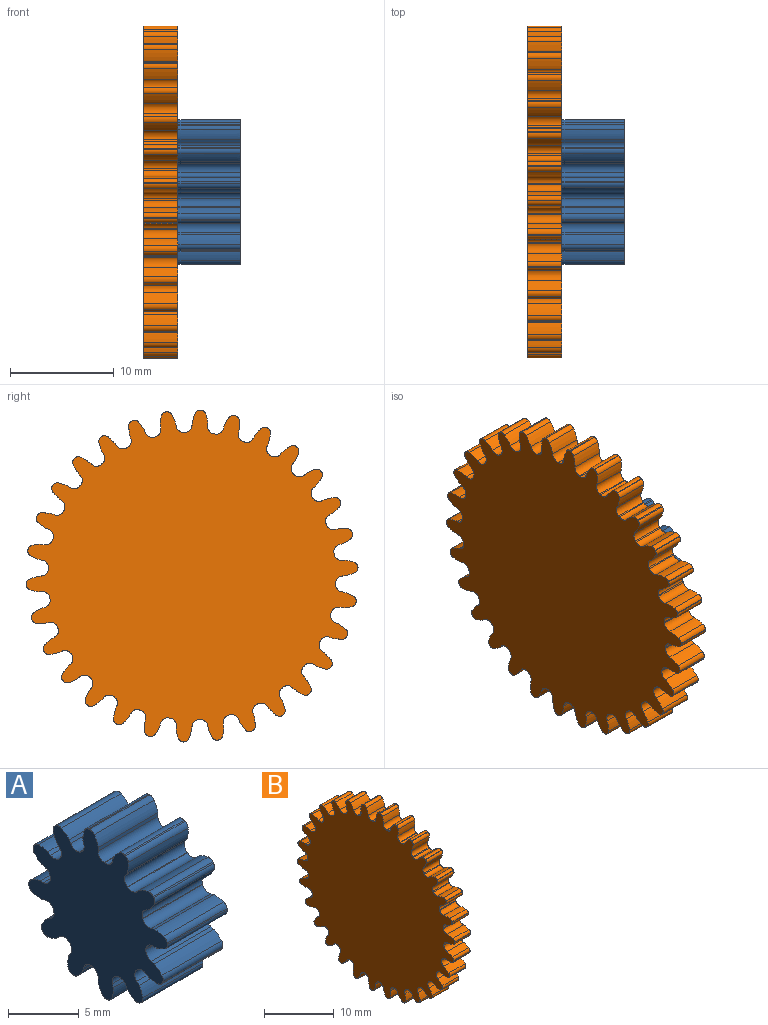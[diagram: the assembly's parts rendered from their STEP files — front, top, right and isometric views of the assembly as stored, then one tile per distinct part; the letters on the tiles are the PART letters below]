
ASSEMBLY  parts=2 mates=1
PART A: 122 faces, bbox 6x13.9x13.9 mm
  f0: cylinder r=4.84mm len=6mm, axis (-1,0,0), area 0.2mm2, adj f72,f73,f75,f76
  f1: plane 6x0.3mm, normal (0,-0.26,0.97), area 1.9mm2, adj f2,f72,f73,f74
  f2: extruded ~6x0.79mm, area 6mm2, adj f1,f72,f73,f98
  f3: cylinder r=7mm len=6mm, axis (-1,0,0), area 0.7mm2, adj f72,f73,f98,f99
  f4: extruded ~6x0.99mm, area 6mm2, adj f5,f72,f73,f99
  f5: plane 6x0.27mm, normal (0,0.5,-0.87), area 1.9mm2, adj f4,f72,f73,f75
  f6: cylinder r=4.84mm len=6mm, axis (-1,0,0), area 0.2mm2, adj f72,f73,f77,f78
  f7: plane 6x0.22mm, normal (0,-0.71,0.71), area 1.9mm2, adj f8,f72,f73,f76
  f8: extruded ~6x0.92mm, area 6mm2, adj f7,f72,f73,f100
  f9: cylinder r=7mm len=6mm, axis (-1,0,0), area 0.7mm2, adj f72,f73,f100,f101
  f10: extruded ~6x0.79mm, area 6mm2, adj f11,f72,f73,f101
  f11: plane 6x0.27mm, normal (0,0.87,-0.5), area 1.9mm2, adj f10,f72,f73,f77
  f12: cylinder r=4.84mm len=6mm, axis (-1,0,0), area 0.2mm2, adj f72,f73,f79,f80
  f13: plane 6x0.3mm, normal (0,-0.97,0.26), area 1.9mm2, adj f14,f72,f73,f78
  f14: extruded ~6x0.99mm, area 6mm2, adj f13,f72,f73,f102
  f15: cylinder r=7mm len=6mm, axis (-1,0,0), area 0.7mm2, adj f72,f73,f102,f103
  f16: extruded ~6x0.92mm, area 6mm2, adj f17,f72,f73,f103
  f17: plane 6x0.31mm, normal (0,1,0), area 1.9mm2, adj f16,f72,f73,f79
  f18: cylinder r=4.84mm len=6mm, axis (-1,0,0), area 0.2mm2, adj f72,f73,f81,f82
  f19: plane 6x0.3mm, normal (0,-0.97,-0.26), area 1.9mm2, adj f20,f72,f73,f80
  f20: extruded ~6x0.79mm, area 6mm2, adj f19,f72,f73,f104
  f21: cylinder r=7mm len=6mm, axis (-1,0,0), area 0.7mm2, adj f72,f73,f104,f105
  f22: extruded ~6x0.99mm, area 6mm2, adj f23,f72,f73,f105
  f23: plane 6x0.27mm, normal (0,0.87,0.5), area 1.9mm2, adj f22,f72,f73,f81
  f24: cylinder r=4.84mm len=6mm, axis (-1,0,0), area 0.2mm2, adj f72,f73,f83,f84
  f25: plane 6x0.22mm, normal (0,-0.71,-0.71), area 1.9mm2, adj f26,f72,f73,f82
  f26: extruded ~6x0.92mm, area 6mm2, adj f25,f72,f73,f106
  f27: cylinder r=7mm len=6mm, axis (-1,0,0), area 0.7mm2, adj f72,f73,f106,f107
  f28: extruded ~6x0.79mm, area 6mm2, adj f29,f72,f73,f107
  f29: plane 6x0.27mm, normal (0,0.5,0.87), area 1.9mm2, adj f28,f72,f73,f83
  f30: cylinder r=4.84mm len=6mm, axis (-1,0,0), area 0.2mm2, adj f72,f73,f85,f86
  f31: plane 6x0.3mm, normal (0,-0.26,-0.97), area 1.9mm2, adj f32,f72,f73,f84
  f32: extruded ~6x0.99mm, area 6mm2, adj f31,f72,f73,f108
  f33: cylinder r=7mm len=6mm, axis (-1,0,0), area 0.7mm2, adj f72,f73,f108,f109
  f34: extruded ~6x0.92mm, area 6mm2, adj f35,f72,f73,f109
  f35: plane 6x0.31mm, normal (0,0,1), area 1.9mm2, adj f34,f72,f73,f85
  f36: cylinder r=4.84mm len=6mm, axis (-1,0,0), area 0.2mm2, adj f72,f73,f87,f88
  f37: plane 6x0.3mm, normal (0,0.26,-0.97), area 1.9mm2, adj f38,f72,f73,f86
  f38: extruded ~6x0.79mm, area 6mm2, adj f37,f72,f73,f110
  f39: cylinder r=7mm len=6mm, axis (-1,0,0), area 0.7mm2, adj f72,f73,f110,f111
  f40: extruded ~6x0.99mm, area 6mm2, adj f41,f72,f73,f111
  f41: plane 6x0.27mm, normal (0,-0.5,0.87), area 1.9mm2, adj f40,f72,f73,f87
  f42: cylinder r=4.84mm len=6mm, axis (-1,0,0), area 0.2mm2, adj f72,f73,f89,f90
  f43: plane 6x0.22mm, normal (0,0.71,-0.71), area 1.9mm2, adj f44,f72,f73,f88
  f44: extruded ~6x0.92mm, area 6mm2, adj f43,f72,f73,f112
  f45: cylinder r=7mm len=6mm, axis (-1,0,0), area 0.7mm2, adj f72,f73,f112,f113
  f46: extruded ~6x0.79mm, area 6mm2, adj f47,f72,f73,f113
  f47: plane 6x0.27mm, normal (0,-0.87,0.5), area 1.9mm2, adj f46,f72,f73,f89
  f48: cylinder r=4.84mm len=6mm, axis (-1,0,0), area 0.2mm2, adj f72,f73,f91,f92
  f49: plane 6x0.3mm, normal (0,0.97,-0.26), area 1.9mm2, adj f50,f72,f73,f90
  f50: extruded ~6x0.99mm, area 6mm2, adj f49,f72,f73,f114
  f51: cylinder r=7mm len=6mm, axis (-1,0,0), area 0.7mm2, adj f72,f73,f114,f115
  f52: extruded ~6x0.92mm, area 6mm2, adj f53,f72,f73,f115
  f53: plane 6x0.31mm, normal (0,-1,0), area 1.9mm2, adj f52,f72,f73,f91
  f54: cylinder r=4.84mm len=6mm, axis (-1,0,0), area 0.2mm2, adj f72,f73,f93,f94
  f55: plane 6x0.3mm, normal (0,0.97,0.26), area 1.9mm2, adj f56,f72,f73,f92
  f56: extruded ~6x0.79mm, area 6mm2, adj f55,f72,f73,f116
  f57: cylinder r=7mm len=6mm, axis (-1,0,0), area 0.7mm2, adj f72,f73,f116,f117
  f58: extruded ~6x0.99mm, area 6mm2, adj f59,f72,f73,f117
  f59: plane 6x0.27mm, normal (0,-0.87,-0.5), area 1.9mm2, adj f58,f72,f73,f93
  f60: cylinder r=4.84mm len=6mm, axis (-1,0,0), area 0.2mm2, adj f72,f73,f95,f96
  f61: plane 6x0.22mm, normal (0,0.71,0.71), area 1.9mm2, adj f62,f72,f73,f94
  f62: extruded ~6x0.92mm, area 6mm2, adj f61,f72,f73,f118
  f63: cylinder r=7mm len=6mm, axis (-1,0,0), area 0.7mm2, adj f72,f73,f118,f119
  f64: extruded ~6x0.79mm, area 6mm2, adj f65,f72,f73,f119
  f65: plane 6x0.27mm, normal (0,-0.5,-0.87), area 1.9mm2, adj f64,f72,f73,f95
  f66: cylinder r=4.84mm len=6mm, axis (-1,0,0), area 0.2mm2, adj f72,f73,f74,f97
  f67: plane 6x0.3mm, normal (0,0.26,0.97), area 1.9mm2, adj f68,f72,f73,f96
  f68: extruded ~6x0.99mm, area 6mm2, adj f67,f72,f73,f120
  f69: cylinder r=7mm len=6mm, axis (-1,0,0), area 0.7mm2, adj f72,f73,f120,f121
  f70: extruded ~6x0.92mm, area 6mm2, adj f71,f72,f73,f121
  f71: plane 6x0.31mm, normal (0,0,-1), area 1.9mm2, adj f70,f72,f73,f97
  f72: plane 13.9x13.9mm, normal (1,0,0), area 109.3mm2, adj f0,f1,f2,f3,f4,f5,f6,f7
  f73: plane 13.9x13.9mm, normal (-1,0,0), area 109.3mm2, adj f0,f1,f2,f3,f4,f5,f6,f7
  f74: cylinder r=0.7mm len=6mm, axis (-1,0,0), area 6.1mm2, adj f1,f66,f72,f73
  f75: cylinder r=0.7mm len=6mm, axis (-1,0,0), area 6.1mm2, adj f0,f5,f72,f73
  f76: cylinder r=0.7mm len=6mm, axis (-1,0,0), area 6.1mm2, adj f0,f7,f72,f73
  f77: cylinder r=0.7mm len=6mm, axis (-1,0,0), area 6.1mm2, adj f6,f11,f72,f73
  f78: cylinder r=0.7mm len=6mm, axis (-1,0,0), area 6.1mm2, adj f6,f13,f72,f73
  f79: cylinder r=0.7mm len=6mm, axis (-1,0,0), area 6.1mm2, adj f12,f17,f72,f73
  f80: cylinder r=0.7mm len=6mm, axis (-1,0,0), area 6.1mm2, adj f12,f19,f72,f73
  f81: cylinder r=0.7mm len=6mm, axis (-1,0,0), area 6.1mm2, adj f18,f23,f72,f73
  f82: cylinder r=0.7mm len=6mm, axis (-1,0,0), area 6.1mm2, adj f18,f25,f72,f73
  f83: cylinder r=0.7mm len=6mm, axis (-1,0,0), area 6.1mm2, adj f24,f29,f72,f73
  f84: cylinder r=0.7mm len=6mm, axis (-1,0,0), area 6.1mm2, adj f24,f31,f72,f73
  f85: cylinder r=0.7mm len=6mm, axis (-1,0,0), area 6.1mm2, adj f30,f35,f72,f73
  f86: cylinder r=0.7mm len=6mm, axis (-1,0,0), area 6.1mm2, adj f30,f37,f72,f73
  f87: cylinder r=0.7mm len=6mm, axis (-1,0,0), area 6.1mm2, adj f36,f41,f72,f73
  f88: cylinder r=0.7mm len=6mm, axis (-1,0,0), area 6.1mm2, adj f36,f43,f72,f73
  f89: cylinder r=0.7mm len=6mm, axis (-1,0,0), area 6.1mm2, adj f42,f47,f72,f73
  f90: cylinder r=0.7mm len=6mm, axis (-1,0,0), area 6.1mm2, adj f42,f49,f72,f73
  f91: cylinder r=0.7mm len=6mm, axis (-1,0,0), area 6.1mm2, adj f48,f53,f72,f73
  f92: cylinder r=0.7mm len=6mm, axis (-1,0,0), area 6.1mm2, adj f48,f55,f72,f73
  f93: cylinder r=0.7mm len=6mm, axis (-1,0,0), area 6.1mm2, adj f54,f59,f72,f73
  f94: cylinder r=0.7mm len=6mm, axis (-1,0,0), area 6.1mm2, adj f54,f61,f72,f73
  f95: cylinder r=0.7mm len=6mm, axis (-1,0,0), area 6.1mm2, adj f60,f65,f72,f73
  f96: cylinder r=0.7mm len=6mm, axis (-1,0,0), area 6.1mm2, adj f60,f67,f72,f73
  f97: cylinder r=0.7mm len=6mm, axis (-1,0,0), area 6.1mm2, adj f66,f71,f72,f73
  f98: cylinder r=0.5mm len=6mm, axis (-1,0,0), area 3.3mm2, adj f2,f3,f72,f73
  f99: cylinder r=0.5mm len=6mm, axis (-1,0,0), area 3.3mm2, adj f3,f4,f72,f73
  f100: cylinder r=0.5mm len=6mm, axis (-1,0,0), area 3.3mm2, adj f8,f9,f72,f73
  f101: cylinder r=0.5mm len=6mm, axis (-1,0,0), area 3.3mm2, adj f9,f10,f72,f73
  f102: cylinder r=0.5mm len=6mm, axis (-1,0,0), area 3.3mm2, adj f14,f15,f72,f73
  f103: cylinder r=0.5mm len=6mm, axis (-1,0,0), area 3.3mm2, adj f15,f16,f72,f73
  f104: cylinder r=0.5mm len=6mm, axis (-1,0,0), area 3.3mm2, adj f20,f21,f72,f73
  f105: cylinder r=0.5mm len=6mm, axis (-1,0,0), area 3.3mm2, adj f21,f22,f72,f73
  f106: cylinder r=0.5mm len=6mm, axis (-1,0,0), area 3.3mm2, adj f26,f27,f72,f73
  f107: cylinder r=0.5mm len=6mm, axis (-1,0,0), area 3.3mm2, adj f27,f28,f72,f73
  f108: cylinder r=0.5mm len=6mm, axis (-1,0,0), area 3.3mm2, adj f32,f33,f72,f73
  f109: cylinder r=0.5mm len=6mm, axis (-1,0,0), area 3.3mm2, adj f33,f34,f72,f73
  f110: cylinder r=0.5mm len=6mm, axis (-1,0,0), area 3.3mm2, adj f38,f39,f72,f73
  f111: cylinder r=0.5mm len=6mm, axis (-1,0,0), area 3.3mm2, adj f39,f40,f72,f73
  f112: cylinder r=0.5mm len=6mm, axis (-1,0,0), area 3.3mm2, adj f44,f45,f72,f73
  f113: cylinder r=0.5mm len=6mm, axis (-1,0,0), area 3.3mm2, adj f45,f46,f72,f73
  f114: cylinder r=0.5mm len=6mm, axis (-1,0,0), area 3.3mm2, adj f50,f51,f72,f73
  f115: cylinder r=0.5mm len=6mm, axis (-1,0,0), area 3.3mm2, adj f51,f52,f72,f73
  f116: cylinder r=0.5mm len=6mm, axis (-1,0,0), area 3.3mm2, adj f56,f57,f72,f73
  f117: cylinder r=0.5mm len=6mm, axis (-1,0,0), area 3.3mm2, adj f57,f58,f72,f73
  f118: cylinder r=0.5mm len=6mm, axis (-1,0,0), area 3.3mm2, adj f62,f63,f72,f73
  f119: cylinder r=0.5mm len=6mm, axis (-1,0,0), area 3.3mm2, adj f63,f64,f72,f73
  f120: cylinder r=0.5mm len=6mm, axis (-1,0,0), area 3.3mm2, adj f68,f69,f72,f73
  f121: cylinder r=0.5mm len=6mm, axis (-1,0,0), area 3.3mm2, adj f69,f70,f72,f73
PART B: 242 faces, bbox 3.3x32x32 mm
  f0: cylinder r=13.84mm len=3.3mm, axis (-1,0,0), area 0.4mm2, adj f120,f121,f123,f124
  f1: extruded ~3.3x1.12mm, area 4mm2, adj f120,f121,f122,f182
  f2: cylinder r=16mm len=3.3mm, axis (-1,0,0), area 0.2mm2, adj f120,f121,f182,f183
  f3: extruded ~3.3x1.2mm, area 4mm2, adj f120,f121,f123,f183
  f4: cylinder r=13.84mm len=3.3mm, axis (-1,0,0), area 0.4mm2, adj f120,f121,f125,f126
  f5: extruded ~3.3x1mm, area 4mm2, adj f120,f121,f124,f184
  f6: cylinder r=16mm len=3.3mm, axis (-1,0,0), area 0.2mm2, adj f120,f121,f184,f185
  f7: extruded ~3.3x1.19mm, area 4mm2, adj f120,f121,f125,f185
  f8: cylinder r=13.84mm len=3.3mm, axis (-1,0,0), area 0.4mm2, adj f120,f121,f127,f128
  f9: extruded ~3.3x0.86mm, area 4mm2, adj f120,f121,f126,f186
  f10: cylinder r=16mm len=3.3mm, axis (-1,0,0), area 0.2mm2, adj f120,f121,f186,f187
  f11: extruded ~3.3x1.12mm, area 4mm2, adj f120,f121,f127,f187
  f12: cylinder r=13.84mm len=3.3mm, axis (-1,0,0), area 0.4mm2, adj f120,f121,f129,f130
  f13: extruded ~3.3x1.01mm, area 4mm2, adj f120,f121,f128,f188
  f14: cylinder r=16mm len=3.3mm, axis (-1,0,0), area 0.2mm2, adj f120,f121,f188,f189
  f15: extruded ~3.3x1.01mm, area 4mm2, adj f120,f121,f129,f189
  f16: cylinder r=13.84mm len=3.3mm, axis (-1,0,0), area 0.4mm2, adj f120,f121,f131,f132
  f17: extruded ~3.3x1.12mm, area 4mm2, adj f120,f121,f130,f190
  f18: cylinder r=16mm len=3.3mm, axis (-1,0,0), area 0.2mm2, adj f120,f121,f190,f191
  f19: extruded ~3.3x0.86mm, area 4mm2, adj f120,f121,f131,f191
  f20: cylinder r=13.84mm len=3.3mm, axis (-1,0,0), area 0.4mm2, adj f120,f121,f133,f134
  f21: extruded ~3.3x1.19mm, area 4mm2, adj f120,f121,f132,f192
  f22: cylinder r=16mm len=3.3mm, axis (-1,0,0), area 0.2mm2, adj f120,f121,f192,f193
  f23: extruded ~3.3x1mm, area 4mm2, adj f120,f121,f133,f193
  f24: cylinder r=13.84mm len=3.3mm, axis (-1,0,0), area 0.4mm2, adj f120,f121,f135,f136
  f25: extruded ~3.3x1.2mm, area 4mm2, adj f120,f121,f134,f194
  f26: cylinder r=16mm len=3.3mm, axis (-1,0,0), area 0.2mm2, adj f120,f121,f194,f195
  f27: extruded ~3.3x1.12mm, area 4mm2, adj f120,f121,f135,f195
  f28: cylinder r=13.84mm len=3.3mm, axis (-1,0,0), area 0.4mm2, adj f120,f121,f137,f138
  f29: extruded ~3.3x1.16mm, area 4mm2, adj f120,f121,f136,f196
  f30: cylinder r=16mm len=3.3mm, axis (-1,0,0), area 0.2mm2, adj f120,f121,f196,f197
  f31: extruded ~3.3x1.18mm, area 4mm2, adj f120,f121,f137,f197
  f32: cylinder r=13.84mm len=3.3mm, axis (-1,0,0), area 0.4mm2, adj f120,f121,f139,f140
  f33: extruded ~3.3x1.06mm, area 4mm2, adj f120,f121,f138,f198
  f34: cylinder r=16mm len=3.3mm, axis (-1,0,0), area 0.2mm2, adj f120,f121,f198,f199
  f35: extruded ~3.3x1.2mm, area 4mm2, adj f120,f121,f139,f199
  f36: cylinder r=13.84mm len=3.3mm, axis (-1,0,0), area 0.4mm2, adj f120,f121,f141,f142
  f37: extruded ~3.3x0.92mm, area 4mm2, adj f120,f121,f140,f200
  f38: cylinder r=16mm len=3.3mm, axis (-1,0,0), area 0.2mm2, adj f120,f121,f200,f201
  f39: extruded ~3.3x1.16mm, area 4mm2, adj f120,f121,f141,f201
  f40: cylinder r=13.84mm len=3.3mm, axis (-1,0,0), area 0.4mm2, adj f120,f121,f143,f144
  f41: extruded ~3.3x0.94mm, area 4mm2, adj f120,f121,f142,f202
  f42: cylinder r=16mm len=3.3mm, axis (-1,0,0), area 0.2mm2, adj f120,f121,f202,f203
  f43: extruded ~3.3x1.07mm, area 4mm2, adj f120,f121,f143,f203
  f44: cylinder r=13.84mm len=3.3mm, axis (-1,0,0), area 0.4mm2, adj f120,f121,f145,f146
  f45: extruded ~3.3x1.07mm, area 4mm2, adj f120,f121,f144,f204
  f46: cylinder r=16mm len=3.3mm, axis (-1,0,0), area 0.2mm2, adj f120,f121,f204,f205
  f47: extruded ~3.3x0.94mm, area 4mm2, adj f120,f121,f145,f205
  f48: cylinder r=13.84mm len=3.3mm, axis (-1,0,0), area 0.4mm2, adj f120,f121,f147,f148
  f49: extruded ~3.3x1.16mm, area 4mm2, adj f120,f121,f146,f206
  f50: cylinder r=16mm len=3.3mm, axis (-1,0,0), area 0.2mm2, adj f120,f121,f206,f207
  f51: extruded ~3.3x0.92mm, area 4mm2, adj f120,f121,f147,f207
  f52: cylinder r=13.84mm len=3.3mm, axis (-1,0,0), area 0.4mm2, adj f120,f121,f149,f150
  f53: extruded ~3.3x1.2mm, area 4mm2, adj f120,f121,f148,f208
  f54: cylinder r=16mm len=3.3mm, axis (-1,0,0), area 0.2mm2, adj f120,f121,f208,f209
  f55: extruded ~3.3x1.06mm, area 4mm2, adj f120,f121,f149,f209
  f56: cylinder r=13.84mm len=3.3mm, axis (-1,0,0), area 0.4mm2, adj f120,f121,f151,f152
  f57: extruded ~3.3x1.18mm, area 4mm2, adj f120,f121,f150,f210
  f58: cylinder r=16mm len=3.3mm, axis (-1,0,0), area 0.2mm2, adj f120,f121,f210,f211
  f59: extruded ~3.3x1.16mm, area 4mm2, adj f120,f121,f151,f211
  f60: cylinder r=13.84mm len=3.3mm, axis (-1,0,0), area 0.4mm2, adj f120,f121,f153,f154
  f61: extruded ~3.3x1.12mm, area 4mm2, adj f120,f121,f152,f212
  f62: cylinder r=16mm len=3.3mm, axis (-1,0,0), area 0.2mm2, adj f120,f121,f212,f213
  f63: extruded ~3.3x1.2mm, area 4mm2, adj f120,f121,f153,f213
  f64: cylinder r=13.84mm len=3.3mm, axis (-1,0,0), area 0.4mm2, adj f120,f121,f155,f156
  f65: extruded ~3.3x1mm, area 4mm2, adj f120,f121,f154,f214
  f66: cylinder r=16mm len=3.3mm, axis (-1,0,0), area 0.2mm2, adj f120,f121,f214,f215
  f67: extruded ~3.3x1.19mm, area 4mm2, adj f120,f121,f155,f215
  f68: cylinder r=13.84mm len=3.3mm, axis (-1,0,0), area 0.4mm2, adj f120,f121,f157,f158
  f69: extruded ~3.3x0.86mm, area 4mm2, adj f120,f121,f156,f216
  f70: cylinder r=16mm len=3.3mm, axis (-1,0,0), area 0.2mm2, adj f120,f121,f216,f217
  f71: extruded ~3.3x1.12mm, area 4mm2, adj f120,f121,f157,f217
  f72: cylinder r=13.84mm len=3.3mm, axis (-1,0,0), area 0.4mm2, adj f120,f121,f159,f160
  f73: extruded ~3.3x1.01mm, area 4mm2, adj f120,f121,f158,f218
  f74: cylinder r=16mm len=3.3mm, axis (-1,0,0), area 0.2mm2, adj f120,f121,f218,f219
  f75: extruded ~3.3x1.01mm, area 4mm2, adj f120,f121,f159,f219
  f76: cylinder r=13.84mm len=3.3mm, axis (-1,0,0), area 0.4mm2, adj f120,f121,f161,f162
  f77: extruded ~3.3x1.12mm, area 4mm2, adj f120,f121,f160,f220
  f78: cylinder r=16mm len=3.3mm, axis (-1,0,0), area 0.2mm2, adj f120,f121,f220,f221
  f79: extruded ~3.3x0.86mm, area 4mm2, adj f120,f121,f161,f221
  f80: cylinder r=13.84mm len=3.3mm, axis (-1,0,0), area 0.4mm2, adj f120,f121,f163,f164
  f81: extruded ~3.3x1.19mm, area 4mm2, adj f120,f121,f162,f222
  f82: cylinder r=16mm len=3.3mm, axis (-1,0,0), area 0.2mm2, adj f120,f121,f222,f223
  f83: extruded ~3.3x1mm, area 4mm2, adj f120,f121,f163,f223
  f84: cylinder r=13.84mm len=3.3mm, axis (-1,0,0), area 0.4mm2, adj f120,f121,f165,f166
  f85: extruded ~3.3x1.2mm, area 4mm2, adj f120,f121,f164,f224
  f86: cylinder r=16mm len=3.3mm, axis (-1,0,0), area 0.2mm2, adj f120,f121,f224,f225
  f87: extruded ~3.3x1.12mm, area 4mm2, adj f120,f121,f165,f225
  f88: cylinder r=13.84mm len=3.3mm, axis (-1,0,0), area 0.4mm2, adj f120,f121,f167,f168
  f89: extruded ~3.3x1.16mm, area 4mm2, adj f120,f121,f166,f226
  f90: cylinder r=16mm len=3.3mm, axis (-1,0,0), area 0.2mm2, adj f120,f121,f226,f227
  f91: extruded ~3.3x1.18mm, area 4mm2, adj f120,f121,f167,f227
  f92: cylinder r=13.84mm len=3.3mm, axis (-1,0,0), area 0.4mm2, adj f120,f121,f169,f170
  f93: extruded ~3.3x1.06mm, area 4mm2, adj f120,f121,f168,f228
  f94: cylinder r=16mm len=3.3mm, axis (-1,0,0), area 0.2mm2, adj f120,f121,f228,f229
  f95: extruded ~3.3x1.2mm, area 4mm2, adj f120,f121,f169,f229
  f96: cylinder r=13.84mm len=3.3mm, axis (-1,0,0), area 0.4mm2, adj f120,f121,f171,f172
  f97: extruded ~3.3x0.92mm, area 4mm2, adj f120,f121,f170,f230
  f98: cylinder r=16mm len=3.3mm, axis (-1,0,0), area 0.2mm2, adj f120,f121,f230,f231
  f99: extruded ~3.3x1.16mm, area 4mm2, adj f120,f121,f171,f231
  f100: cylinder r=13.84mm len=3.3mm, axis (-1,0,0), area 0.4mm2, adj f120,f121,f173,f174
  f101: extruded ~3.3x0.94mm, area 4mm2, adj f120,f121,f172,f232
  f102: cylinder r=16mm len=3.3mm, axis (-1,0,0), area 0.2mm2, adj f120,f121,f232,f233
  f103: extruded ~3.3x1.07mm, area 4mm2, adj f120,f121,f173,f233
  f104: cylinder r=13.84mm len=3.3mm, axis (-1,0,0), area 0.4mm2, adj f120,f121,f175,f176
  f105: extruded ~3.3x1.07mm, area 4mm2, adj f120,f121,f174,f234
  f106: cylinder r=16mm len=3.3mm, axis (-1,0,0), area 0.2mm2, adj f120,f121,f234,f235
  f107: extruded ~3.3x0.94mm, area 4mm2, adj f120,f121,f175,f235
  f108: cylinder r=13.84mm len=3.3mm, axis (-1,0,0), area 0.4mm2, adj f120,f121,f177,f178
  f109: extruded ~3.3x1.16mm, area 4mm2, adj f120,f121,f176,f236
  f110: cylinder r=16mm len=3.3mm, axis (-1,0,0), area 0.2mm2, adj f120,f121,f236,f237
  f111: extruded ~3.3x0.92mm, area 4mm2, adj f120,f121,f177,f237
  f112: cylinder r=13.84mm len=3.3mm, axis (-1,0,0), area 0.4mm2, adj f120,f121,f179,f180
  f113: extruded ~3.3x1.2mm, area 4mm2, adj f120,f121,f178,f238
  f114: cylinder r=16mm len=3.3mm, axis (-1,0,0), area 0.2mm2, adj f120,f121,f238,f239
  f115: extruded ~3.3x1.06mm, area 4mm2, adj f120,f121,f179,f239
  f116: cylinder r=13.84mm len=3.3mm, axis (-1,0,0), area 0.4mm2, adj f120,f121,f122,f181
  f117: extruded ~3.3x1.18mm, area 4mm2, adj f120,f121,f180,f240
  f118: cylinder r=16mm len=3.3mm, axis (-1,0,0), area 0.2mm2, adj f120,f121,f240,f241
  f119: extruded ~3.3x1.16mm, area 4mm2, adj f120,f121,f181,f241
  f120: plane 31.96x31.96mm, normal (1,0,0), area 691.4mm2, adj f0,f1,f2,f3,f4,f5,f6,f7
  f121: plane 31.96x31.96mm, normal (-1,0,0), area 691.4mm2, adj f0,f1,f2,f3,f4,f5,f6,f7
  f122: cylinder r=0.7mm len=3.3mm, axis (-1,0,0), area 3.5mm2, adj f1,f116,f120,f121
  f123: cylinder r=0.7mm len=3.3mm, axis (-1,0,0), area 3.5mm2, adj f0,f3,f120,f121
  f124: cylinder r=0.7mm len=3.3mm, axis (-1,0,0), area 3.5mm2, adj f0,f5,f120,f121
  f125: cylinder r=0.7mm len=3.3mm, axis (-1,0,0), area 3.5mm2, adj f4,f7,f120,f121
  f126: cylinder r=0.7mm len=3.3mm, axis (-1,0,0), area 3.5mm2, adj f4,f9,f120,f121
  f127: cylinder r=0.7mm len=3.3mm, axis (-1,0,0), area 3.5mm2, adj f8,f11,f120,f121
  f128: cylinder r=0.7mm len=3.3mm, axis (-1,0,0), area 3.5mm2, adj f8,f13,f120,f121
  f129: cylinder r=0.7mm len=3.3mm, axis (-1,0,0), area 3.5mm2, adj f12,f15,f120,f121
  f130: cylinder r=0.7mm len=3.3mm, axis (-1,0,0), area 3.5mm2, adj f12,f17,f120,f121
  f131: cylinder r=0.7mm len=3.3mm, axis (-1,0,0), area 3.5mm2, adj f16,f19,f120,f121
  f132: cylinder r=0.7mm len=3.3mm, axis (-1,0,0), area 3.5mm2, adj f16,f21,f120,f121
  f133: cylinder r=0.7mm len=3.3mm, axis (-1,0,0), area 3.5mm2, adj f20,f23,f120,f121
  f134: cylinder r=0.7mm len=3.3mm, axis (-1,0,0), area 3.5mm2, adj f20,f25,f120,f121
  f135: cylinder r=0.7mm len=3.3mm, axis (-1,0,0), area 3.5mm2, adj f24,f27,f120,f121
  f136: cylinder r=0.7mm len=3.3mm, axis (-1,0,0), area 3.5mm2, adj f24,f29,f120,f121
  f137: cylinder r=0.7mm len=3.3mm, axis (-1,0,0), area 3.5mm2, adj f28,f31,f120,f121
  f138: cylinder r=0.7mm len=3.3mm, axis (-1,0,0), area 3.5mm2, adj f28,f33,f120,f121
  f139: cylinder r=0.7mm len=3.3mm, axis (-1,0,0), area 3.5mm2, adj f32,f35,f120,f121
  f140: cylinder r=0.7mm len=3.3mm, axis (-1,0,0), area 3.5mm2, adj f32,f37,f120,f121
  f141: cylinder r=0.7mm len=3.3mm, axis (-1,0,0), area 3.5mm2, adj f36,f39,f120,f121
  f142: cylinder r=0.7mm len=3.3mm, axis (-1,0,0), area 3.5mm2, adj f36,f41,f120,f121
  f143: cylinder r=0.7mm len=3.3mm, axis (-1,0,0), area 3.5mm2, adj f40,f43,f120,f121
  f144: cylinder r=0.7mm len=3.3mm, axis (-1,0,0), area 3.5mm2, adj f40,f45,f120,f121
  f145: cylinder r=0.7mm len=3.3mm, axis (-1,0,0), area 3.5mm2, adj f44,f47,f120,f121
  f146: cylinder r=0.7mm len=3.3mm, axis (-1,0,0), area 3.5mm2, adj f44,f49,f120,f121
  f147: cylinder r=0.7mm len=3.3mm, axis (-1,0,0), area 3.5mm2, adj f48,f51,f120,f121
  f148: cylinder r=0.7mm len=3.3mm, axis (-1,0,0), area 3.5mm2, adj f48,f53,f120,f121
  f149: cylinder r=0.7mm len=3.3mm, axis (-1,0,0), area 3.5mm2, adj f52,f55,f120,f121
  f150: cylinder r=0.7mm len=3.3mm, axis (-1,0,0), area 3.5mm2, adj f52,f57,f120,f121
  f151: cylinder r=0.7mm len=3.3mm, axis (-1,0,0), area 3.5mm2, adj f56,f59,f120,f121
  f152: cylinder r=0.7mm len=3.3mm, axis (-1,0,0), area 3.5mm2, adj f56,f61,f120,f121
  f153: cylinder r=0.7mm len=3.3mm, axis (-1,0,0), area 3.5mm2, adj f60,f63,f120,f121
  f154: cylinder r=0.7mm len=3.3mm, axis (-1,0,0), area 3.5mm2, adj f60,f65,f120,f121
  f155: cylinder r=0.7mm len=3.3mm, axis (-1,0,0), area 3.5mm2, adj f64,f67,f120,f121
  f156: cylinder r=0.7mm len=3.3mm, axis (-1,0,0), area 3.5mm2, adj f64,f69,f120,f121
  f157: cylinder r=0.7mm len=3.3mm, axis (-1,0,0), area 3.5mm2, adj f68,f71,f120,f121
  f158: cylinder r=0.7mm len=3.3mm, axis (-1,0,0), area 3.5mm2, adj f68,f73,f120,f121
  f159: cylinder r=0.7mm len=3.3mm, axis (-1,0,0), area 3.5mm2, adj f72,f75,f120,f121
  f160: cylinder r=0.7mm len=3.3mm, axis (-1,0,0), area 3.5mm2, adj f72,f77,f120,f121
  f161: cylinder r=0.7mm len=3.3mm, axis (-1,0,0), area 3.5mm2, adj f76,f79,f120,f121
  f162: cylinder r=0.7mm len=3.3mm, axis (-1,0,0), area 3.5mm2, adj f76,f81,f120,f121
  f163: cylinder r=0.7mm len=3.3mm, axis (-1,0,0), area 3.5mm2, adj f80,f83,f120,f121
  f164: cylinder r=0.7mm len=3.3mm, axis (-1,0,0), area 3.5mm2, adj f80,f85,f120,f121
  f165: cylinder r=0.7mm len=3.3mm, axis (-1,0,0), area 3.5mm2, adj f84,f87,f120,f121
  f166: cylinder r=0.7mm len=3.3mm, axis (-1,0,0), area 3.5mm2, adj f84,f89,f120,f121
  f167: cylinder r=0.7mm len=3.3mm, axis (-1,0,0), area 3.5mm2, adj f88,f91,f120,f121
  f168: cylinder r=0.7mm len=3.3mm, axis (-1,0,0), area 3.5mm2, adj f88,f93,f120,f121
  f169: cylinder r=0.7mm len=3.3mm, axis (-1,0,0), area 3.5mm2, adj f92,f95,f120,f121
  f170: cylinder r=0.7mm len=3.3mm, axis (-1,0,0), area 3.5mm2, adj f92,f97,f120,f121
  f171: cylinder r=0.7mm len=3.3mm, axis (-1,0,0), area 3.5mm2, adj f96,f99,f120,f121
  f172: cylinder r=0.7mm len=3.3mm, axis (-1,0,0), area 3.5mm2, adj f96,f101,f120,f121
  f173: cylinder r=0.7mm len=3.3mm, axis (-1,0,0), area 3.5mm2, adj f100,f103,f120,f121
  f174: cylinder r=0.7mm len=3.3mm, axis (-1,0,0), area 3.5mm2, adj f100,f105,f120,f121
  f175: cylinder r=0.7mm len=3.3mm, axis (-1,0,0), area 3.5mm2, adj f104,f107,f120,f121
  f176: cylinder r=0.7mm len=3.3mm, axis (-1,0,0), area 3.5mm2, adj f104,f109,f120,f121
  f177: cylinder r=0.7mm len=3.3mm, axis (-1,0,0), area 3.5mm2, adj f108,f111,f120,f121
  f178: cylinder r=0.7mm len=3.3mm, axis (-1,0,0), area 3.5mm2, adj f108,f113,f120,f121
  f179: cylinder r=0.7mm len=3.3mm, axis (-1,0,0), area 3.5mm2, adj f112,f115,f120,f121
  f180: cylinder r=0.7mm len=3.3mm, axis (-1,0,0), area 3.5mm2, adj f112,f117,f120,f121
  f181: cylinder r=0.7mm len=3.3mm, axis (-1,0,0), area 3.5mm2, adj f116,f119,f120,f121
  f182: cylinder r=0.5mm len=3.3mm, axis (-1,0,0), area 2mm2, adj f1,f2,f120,f121
  f183: cylinder r=0.5mm len=3.3mm, axis (-1,0,0), area 2mm2, adj f2,f3,f120,f121
  f184: cylinder r=0.5mm len=3.3mm, axis (-1,0,0), area 2mm2, adj f5,f6,f120,f121
  f185: cylinder r=0.5mm len=3.3mm, axis (-1,0,0), area 2mm2, adj f6,f7,f120,f121
  f186: cylinder r=0.5mm len=3.3mm, axis (-1,0,0), area 2mm2, adj f9,f10,f120,f121
  f187: cylinder r=0.5mm len=3.3mm, axis (-1,0,0), area 2mm2, adj f10,f11,f120,f121
  f188: cylinder r=0.5mm len=3.3mm, axis (-1,0,0), area 2mm2, adj f13,f14,f120,f121
  f189: cylinder r=0.5mm len=3.3mm, axis (-1,0,0), area 2mm2, adj f14,f15,f120,f121
  f190: cylinder r=0.5mm len=3.3mm, axis (-1,0,0), area 2mm2, adj f17,f18,f120,f121
  f191: cylinder r=0.5mm len=3.3mm, axis (-1,0,0), area 2mm2, adj f18,f19,f120,f121
  f192: cylinder r=0.5mm len=3.3mm, axis (-1,0,0), area 2mm2, adj f21,f22,f120,f121
  f193: cylinder r=0.5mm len=3.3mm, axis (-1,0,0), area 2mm2, adj f22,f23,f120,f121
  f194: cylinder r=0.5mm len=3.3mm, axis (-1,0,0), area 2mm2, adj f25,f26,f120,f121
  f195: cylinder r=0.5mm len=3.3mm, axis (-1,0,0), area 2mm2, adj f26,f27,f120,f121
  f196: cylinder r=0.5mm len=3.3mm, axis (-1,0,0), area 2mm2, adj f29,f30,f120,f121
  f197: cylinder r=0.5mm len=3.3mm, axis (-1,0,0), area 2mm2, adj f30,f31,f120,f121
  f198: cylinder r=0.5mm len=3.3mm, axis (-1,0,0), area 2mm2, adj f33,f34,f120,f121
  f199: cylinder r=0.5mm len=3.3mm, axis (-1,0,0), area 2mm2, adj f34,f35,f120,f121
  f200: cylinder r=0.5mm len=3.3mm, axis (-1,0,0), area 2mm2, adj f37,f38,f120,f121
  f201: cylinder r=0.5mm len=3.3mm, axis (-1,0,0), area 2mm2, adj f38,f39,f120,f121
  f202: cylinder r=0.5mm len=3.3mm, axis (-1,0,0), area 2mm2, adj f41,f42,f120,f121
  f203: cylinder r=0.5mm len=3.3mm, axis (-1,0,0), area 2mm2, adj f42,f43,f120,f121
  f204: cylinder r=0.5mm len=3.3mm, axis (-1,0,0), area 2mm2, adj f45,f46,f120,f121
  f205: cylinder r=0.5mm len=3.3mm, axis (-1,0,0), area 2mm2, adj f46,f47,f120,f121
  f206: cylinder r=0.5mm len=3.3mm, axis (-1,0,0), area 2mm2, adj f49,f50,f120,f121
  f207: cylinder r=0.5mm len=3.3mm, axis (-1,0,0), area 2mm2, adj f50,f51,f120,f121
  f208: cylinder r=0.5mm len=3.3mm, axis (-1,0,0), area 2mm2, adj f53,f54,f120,f121
  f209: cylinder r=0.5mm len=3.3mm, axis (-1,0,0), area 2mm2, adj f54,f55,f120,f121
  f210: cylinder r=0.5mm len=3.3mm, axis (-1,0,0), area 2mm2, adj f57,f58,f120,f121
  f211: cylinder r=0.5mm len=3.3mm, axis (-1,0,0), area 2mm2, adj f58,f59,f120,f121
  f212: cylinder r=0.5mm len=3.3mm, axis (-1,0,0), area 2mm2, adj f61,f62,f120,f121
  f213: cylinder r=0.5mm len=3.3mm, axis (-1,0,0), area 2mm2, adj f62,f63,f120,f121
  f214: cylinder r=0.5mm len=3.3mm, axis (-1,0,0), area 2mm2, adj f65,f66,f120,f121
  f215: cylinder r=0.5mm len=3.3mm, axis (-1,0,0), area 2mm2, adj f66,f67,f120,f121
  f216: cylinder r=0.5mm len=3.3mm, axis (-1,0,0), area 2mm2, adj f69,f70,f120,f121
  f217: cylinder r=0.5mm len=3.3mm, axis (-1,0,0), area 2mm2, adj f70,f71,f120,f121
  f218: cylinder r=0.5mm len=3.3mm, axis (-1,0,0), area 2mm2, adj f73,f74,f120,f121
  f219: cylinder r=0.5mm len=3.3mm, axis (-1,0,0), area 2mm2, adj f74,f75,f120,f121
  f220: cylinder r=0.5mm len=3.3mm, axis (-1,0,0), area 2mm2, adj f77,f78,f120,f121
  f221: cylinder r=0.5mm len=3.3mm, axis (-1,0,0), area 2mm2, adj f78,f79,f120,f121
  f222: cylinder r=0.5mm len=3.3mm, axis (-1,0,0), area 2mm2, adj f81,f82,f120,f121
  f223: cylinder r=0.5mm len=3.3mm, axis (-1,0,0), area 2mm2, adj f82,f83,f120,f121
  f224: cylinder r=0.5mm len=3.3mm, axis (-1,0,0), area 2mm2, adj f85,f86,f120,f121
  f225: cylinder r=0.5mm len=3.3mm, axis (-1,0,0), area 2mm2, adj f86,f87,f120,f121
  f226: cylinder r=0.5mm len=3.3mm, axis (-1,0,0), area 2mm2, adj f89,f90,f120,f121
  f227: cylinder r=0.5mm len=3.3mm, axis (-1,0,0), area 2mm2, adj f90,f91,f120,f121
  f228: cylinder r=0.5mm len=3.3mm, axis (-1,0,0), area 2mm2, adj f93,f94,f120,f121
  f229: cylinder r=0.5mm len=3.3mm, axis (-1,0,0), area 2mm2, adj f94,f95,f120,f121
  f230: cylinder r=0.5mm len=3.3mm, axis (-1,0,0), area 2mm2, adj f97,f98,f120,f121
  f231: cylinder r=0.5mm len=3.3mm, axis (-1,0,0), area 2mm2, adj f98,f99,f120,f121
  f232: cylinder r=0.5mm len=3.3mm, axis (-1,0,0), area 2mm2, adj f101,f102,f120,f121
  f233: cylinder r=0.5mm len=3.3mm, axis (-1,0,0), area 2mm2, adj f102,f103,f120,f121
  f234: cylinder r=0.5mm len=3.3mm, axis (-1,0,0), area 2mm2, adj f105,f106,f120,f121
  f235: cylinder r=0.5mm len=3.3mm, axis (-1,0,0), area 2mm2, adj f106,f107,f120,f121
  f236: cylinder r=0.5mm len=3.3mm, axis (-1,0,0), area 2mm2, adj f109,f110,f120,f121
  f237: cylinder r=0.5mm len=3.3mm, axis (-1,0,0), area 2mm2, adj f110,f111,f120,f121
  f238: cylinder r=0.5mm len=3.3mm, axis (-1,0,0), area 2mm2, adj f113,f114,f120,f121
  f239: cylinder r=0.5mm len=3.3mm, axis (-1,0,0), area 2mm2, adj f114,f115,f120,f121
  f240: cylinder r=0.5mm len=3.3mm, axis (-1,0,0), area 2mm2, adj f117,f118,f120,f121
  f241: cylinder r=0.5mm len=3.3mm, axis (-1,0,0), area 2mm2, adj f118,f119,f120,f121
PLACE A t=(3.3,0,0)mm
PLACE B at identity
MATE fastened A.f0 <-> B.f0  axis (-1,0,0) through (6.6,0,0)mm
